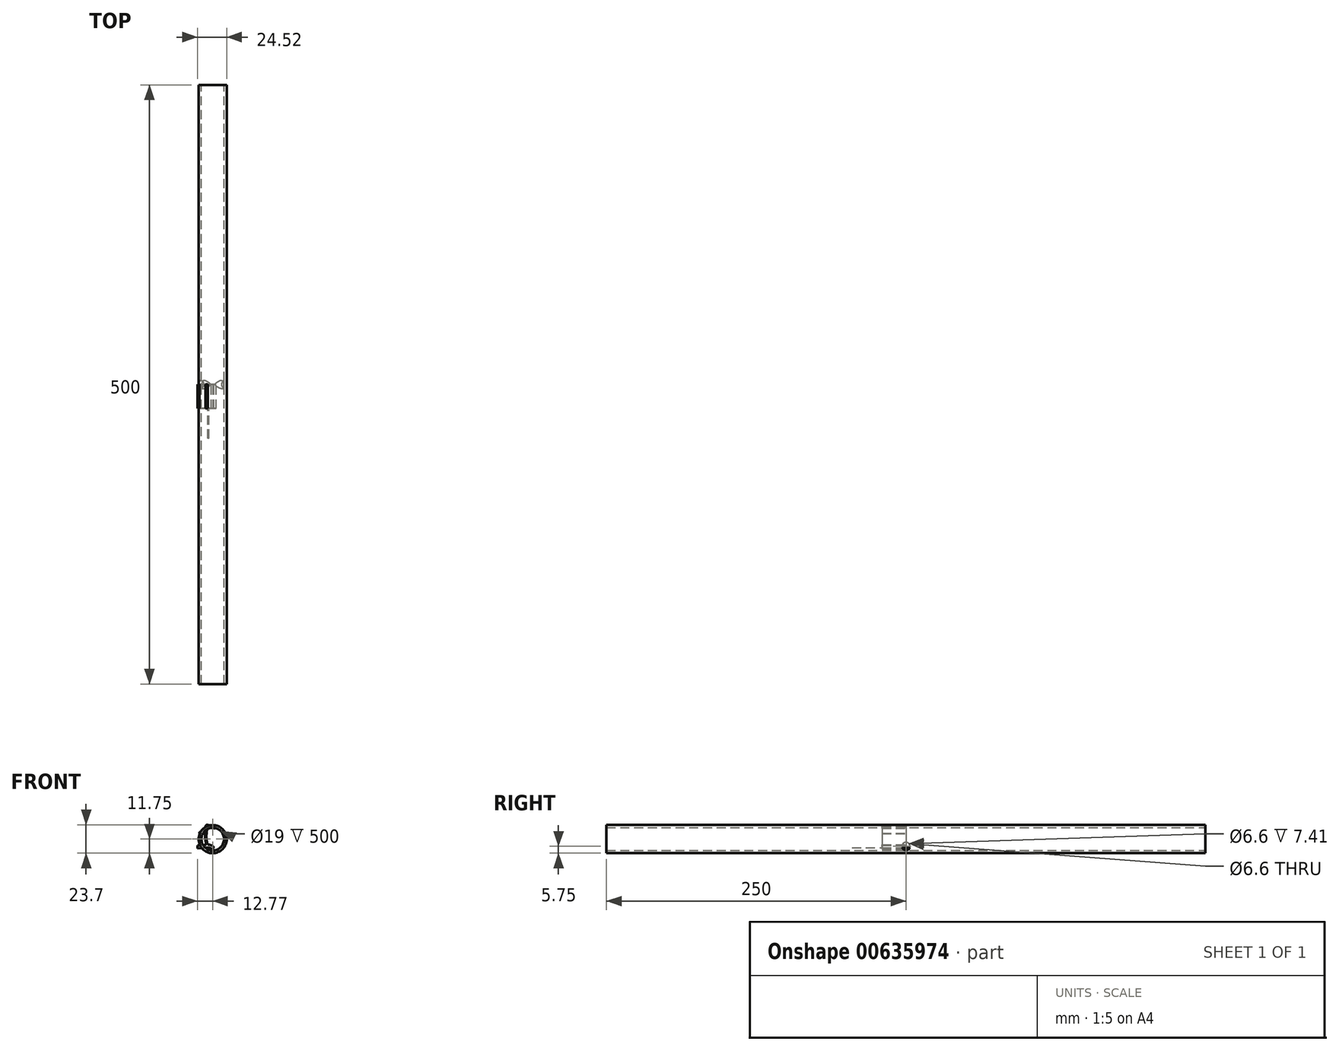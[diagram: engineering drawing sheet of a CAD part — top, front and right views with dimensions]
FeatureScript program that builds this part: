
annotation { "Feature Type Name" : "Feature", "Feature Type Description" : "" }
export const myFeature = defineFeature(function(context is Context, id is Id, definition is map)
    precondition{}
    {
        {
            var Q0;
            Q0=qCreatedBy(makeId("Front.planeOp"),FACE);
            var sketch = newSketch(context, id + "F0", { "sketchPlane" : qUnion([Q0])});
            skCircle(sketch, "E0", {"center": v(0, 0) * mm, "radius": 9.5 * mm});
            skCircle(sketch, "E1", {"center": v(0, 0) * mm, "radius": 11.75 * mm});
            skSolve(sketch);
        }
        {
            var Q0;
            Q0=makeQuery(id+"F0.imprint","IMPRINT",FACE,{"disambiguationData":[TD([[makeQuery(id+"F0.imprint","IMPRINT",EDGE,{"derivedFrom":sQuery(id+"F0.wireOp",EDGE,"E0")}),-1.0]])]});
            extrude(context, id + "F1", {"entities" : qUnion([Q0]), "depth" : 500 * mm, "offsetDistance" : 25 * mm, "symmetric" : true});
        }
        {
            var Q0;
            Q0=qCreatedBy(makeId("Front.planeOp"),FACE);
            var sketch = newSketch(context, id + "F2", { "sketchPlane" : qUnion([Q0])});
            skLineSegment(sketch, "E2.bottom", {"start": v(9.35, 12) * mm, "end": v(-9.35, 12) * mm});
            skLineSegment(sketch, "E2.top", {"start": v(9.35, -12) * mm, "end": v(-9.35, -12) * mm});
            skLineSegment(sketch, "E2.left", {"start": v(9.35, 12) * mm, "end": v(9.35, -12) * mm});
            skLineSegment(sketch, "E2.right", {"start": v(-9.35, 3.53) * mm, "end": v(-9.35, -12) * mm});
            skPoint(sketch, "E2.middle", {"position": v(0, 0) * mm});
            skLineSegment(sketch, "E3", {"start": v(-18.96, 6) * mm, "end": v(16.45, 6) * mm, "construction": true});
            skLineSegment(sketch, "E4", {"start": v(-9.35, 3.53) * mm, "end": v(-15.81, 7.76) * mm});
            skLineSegment(sketch, "E5", {"start": v(-15.81, 7.76) * mm, "end": v(-15.81, 12) * mm});
            skLineSegment(sketch, "E6", {"start": v(-15.81, 12) * mm, "end": v(-9.35, 12) * mm});
            skSolve(sketch);
        }
        {
            var Q0;
            Q0=makeQuery(id+"F2.imprint","IMPRINT",FACE,{"disambiguationData":[TD([[makeQuery(id+"F2.imprint","IMPRINT",EDGE,{"derivedFrom":sQuery(id+"F2.wireOp",EDGE,"E2.bottom")}),1.0]])]});
            extrude(context, id + "F3", {"entities" : qUnion([Q0]), "depth" : 12 * mm, "offsetDistance" : 25 * mm, "symmetric" : true});
        }
        {
            var Q0;
            Q0=makeQuery(id+"F3.opExtrude","SWEPT_FACE",FACE,{"disambiguationData":[OSD([sQuery(id+"F2.wireOp",EDGE,"E2.left")])]});
            var sketch = newSketch(context, id + "F4", { "sketchPlane" : qUnion([Q0])});
            skLineSegment(sketch, "E7", {"start": v(-13.9, -6) * mm, "end": v(15.88, -6) * mm, "construction": true});
            skLineSegment(sketch, "E8", {"start": v(0, -15.68) * mm, "end": v(0, 14.93) * mm, "construction": true});
            skCircle(sketch, "E9", {"center": v(0, -6) * mm, "radius": 3.3 * mm});
            skSolve(sketch);
        }
        {
            var Q0;
            Q0=makeQuery(id+"F4.imprint","IMPRINT",FACE,{"disambiguationData":[TD([[makeQuery(id+"F4.imprint","IMPRINT",EDGE,{"derivedFrom":sQuery(id+"F4.wireOp",EDGE,"E9")}),1.0]])]});
            extrude(context, id + "F5", {"entities" : qUnion([Q0]), "operationType" : NewBodyOperationType.REMOVE, "endBound" : BoundingType.THROUGH_ALL, "oppositeDirection" : true, "depth" : 25 * mm, "offsetDistance" : 25 * mm});
        }
        {
            var Q0;
            Q0=makeQuery(id+"F3.opExtrude","CAP_EDGE",EDGE,{"disambiguationData":[OSD([sQuery(id+"F2.wireOp",EDGE,"E4")])],"isStart":false});
            var Q1;
            Q1=makeQuery(id+"F3.opExtrude","CAP_EDGE",EDGE,{"disambiguationData":[OSD([sQuery(id+"F2.wireOp",EDGE,"E5")])],"isStart":false});
            var Q2;
            Q2=makeQuery(id+"F3.opExtrude","CAP_EDGE",EDGE,{"disambiguationData":[OSD([sQuery(id+"F2.wireOp",EDGE,"E2.bottom"),sQuery(id+"F2.wireOp",EDGE,"E6")])],"isStart":false});
            var Q3;
            Q3=makeQuery(id+"F3.opExtrude","CAP_EDGE",EDGE,{"disambiguationData":[OSD([sQuery(id+"F2.wireOp",EDGE,"E2.left")])],"isStart":false});
            var Q4;
            Q4=makeQuery(id+"F3.opExtrude","CAP_EDGE",EDGE,{"disambiguationData":[OSD([sQuery(id+"F2.wireOp",EDGE,"E2.top")])],"isStart":false});
            var Q5;
            Q5=makeQuery(id+"F3.opExtrude","CAP_EDGE",EDGE,{"disambiguationData":[OSD([sQuery(id+"F2.wireOp",EDGE,"E2.right")])],"isStart":false});
            var Q6;
            Q6=makeQuery(id+"F3.opExtrude","CAP_EDGE",EDGE,{"disambiguationData":[OSD([sQuery(id+"F2.wireOp",EDGE,"E4")])],"isStart":true});
            var Q7;
            Q7=makeQuery(id+"F3.opExtrude","CAP_EDGE",EDGE,{"disambiguationData":[OSD([sQuery(id+"F2.wireOp",EDGE,"E2.right")])],"isStart":true});
            var Q8;
            Q8=makeQuery(id+"F3.opExtrude","CAP_EDGE",EDGE,{"disambiguationData":[OSD([sQuery(id+"F2.wireOp",EDGE,"E2.top")])],"isStart":true});
            var Q9;
            Q9=makeQuery(id+"F3.opExtrude","CAP_EDGE",EDGE,{"disambiguationData":[OSD([sQuery(id+"F2.wireOp",EDGE,"E2.left")])],"isStart":true});
            var Q10;
            Q10=makeQuery(id+"F3.opExtrude","CAP_EDGE",EDGE,{"disambiguationData":[OSD([sQuery(id+"F2.wireOp",EDGE,"E2.bottom"),sQuery(id+"F2.wireOp",EDGE,"E6")])],"isStart":true});
            var Q11;
            Q11=makeQuery(id+"F3.opExtrude","CAP_EDGE",EDGE,{"disambiguationData":[OSD([sQuery(id+"F2.wireOp",EDGE,"E5")])],"isStart":true});
            var Q12;
            Q12=makeQuery(id+"F3.opExtrude","SWEPT_EDGE",EDGE,{"disambiguationData":[OSD([sQuery(id+"F2.wireOp",EDGE,"E2.bottom"),sQuery(id+"F2.wireOp",EDGE,"E2.left")])]});
            var Q13;
            Q13=makeQuery(id+"F3.opExtrude","SWEPT_EDGE",EDGE,{"disambiguationData":[OSD([sQuery(id+"F2.wireOp",EDGE,"E5"),sQuery(id+"F2.wireOp",EDGE,"E6")])]});
            var Q14;
            Q14=makeQuery(id+"F3.opExtrude","SWEPT_EDGE",EDGE,{"disambiguationData":[OSD([sQuery(id+"F2.wireOp",EDGE,"E2.top"),sQuery(id+"F2.wireOp",EDGE,"E2.right")])]});
            var Q15;
            Q15=makeQuery(id+"F3.opExtrude","SWEPT_EDGE",EDGE,{"disambiguationData":[OSD([sQuery(id+"F2.wireOp",EDGE,"E2.top"),sQuery(id+"F2.wireOp",EDGE,"E2.left")])]});
            var Q16;
            Q16=makeQuery(id+"F3.opExtrude","SWEPT_EDGE",EDGE,{"disambiguationData":[OSD([sQuery(id+"F2.wireOp",EDGE,"E4"),sQuery(id+"F2.wireOp",EDGE,"E5")])]});
            var Q17;
            Q17=makeQuery(id+"F3.opExtrude","SWEPT_EDGE",EDGE,{"disambiguationData":[OSD([sQuery(id+"F2.wireOp",EDGE,"E2.right"),sQuery(id+"F2.wireOp",EDGE,"E4")])]});
            fillet(context, id + "F6", {"entities" : qUnion([Q0, Q1, Q2, Q3, Q4, Q5, Q6, Q7, Q8, Q9, Q10, Q11, Q12, Q13, Q14, Q15, Q16, Q17]), "radius" : 1 * mm, "tangentPropagation" : true, "allowEdgeOverflow" : false});
        }
        {
            var Q0;
            Q0=qCreatedBy(makeId("Front.planeOp"),FACE);
            var sketch = newSketch(context, id + "F7", { "sketchPlane" : qUnion([Q0])});
            skLineSegment(sketch, "E10.bottom", {"start": v(4.25, 9.5) * mm, "end": v(-4.25, 9.5) * mm, "construction": true});
            skLineSegment(sketch, "E10.top", {"start": v(4.25, -9.5) * mm, "end": v(-4.25, -9.5) * mm, "construction": true});
            skLineSegment(sketch, "E10.left", {"start": v(4.25, 9.5) * mm, "end": v(4.25, -9.5) * mm, "construction": true});
            skLineSegment(sketch, "E10.right", {"start": v(-4.25, 9.5) * mm, "end": v(-4.25, -4.65) * mm, "construction": true});
            skPoint(sketch, "E10.middle", {"position": v(0, 0) * mm});
            skLineSegment(sketch, "E11.0", {"start": v(3.75, 9) * mm, "end": v(-3.75, 9) * mm, "construction": true});
            skLineSegment(sketch, "E11.1", {"start": v(3.75, 9) * mm, "end": v(3.75, -9) * mm, "construction": true});
            skLineSegment(sketch, "E11.2", {"start": v(3.75, -9) * mm, "end": v(-3.73, -9) * mm, "construction": true});
            skLineSegment(sketch, "E11.3", {"start": v(-3.75, 9) * mm, "end": v(-3.75, -4) * mm, "construction": true});
            skLineSegment(sketch, "E12", {"start": v(-3.75, -4.65) * mm, "end": v(0.77, -4.65) * mm, "construction": true});
            skLineSegment(sketch, "E13", {"start": v(0.77, -4.65) * mm, "end": v(0.77, -8.36) * mm, "construction": true});
            skLineSegment(sketch, "E14", {"start": v(0.77, -8.36) * mm, "end": v(-4.25, -7.75) * mm, "construction": true});
            skLineSegment(sketch, "E15.trimOffspring", {"start": v(-4.25, -7.75) * mm, "end": v(-4.25, -9.5) * mm, "construction": true});
            skLineSegment(sketch, "E16.0", {"start": v(-8.27, -9.5) * mm, "end": v(9.76, -9.5) * mm});
            skLineSegment(sketch, "E17.0", {"start": v(-3.75, -4) * mm, "end": v(1.28, -4) * mm, "construction": true});
            skArc(sketch, "E18", {"start": v(-0.65, -8.19) * mm, "mid": v(0.66, -7.4) * mm, "end": v(0.23, -5.93) * mm});
            skLineSegment(sketch, "E19.0", {"start": v(0.7, -8.85) * mm, "end": v(-3.73, -8.32) * mm, "construction": true});
            skLineSegment(sketch, "E20", {"start": v(-4.25, -4.65) * mm, "end": v(-3.75, -4.65) * mm, "construction": true});
            skLineSegment(sketch, "E21.trimOffspring", {"start": v(-3.73, -8.32) * mm, "end": v(-3.73, -9) * mm, "construction": true});
            skLineSegment(sketch, "E22", {"start": v(0.7, -8.85) * mm, "end": v(1.28, -8.85) * mm, "construction": true});
            skLineSegment(sketch, "E23.trimOffspring", {"start": v(1.28, -4) * mm, "end": v(1.28, -8.85) * mm, "construction": true});
            skLineSegment(sketch, "E24", {"start": v(-5.25, -10.27) * mm, "end": v(-5.25, 10.17) * mm, "construction": true});
            skArc(sketch, "E25", {"start": v(0.23, -5.93) * mm, "mid": v(-1.66, -4.98) * mm, "end": v(-3.75, -4.65) * mm});
            skPoint(sketch, "E26", {"position": v(-5.25, 2.43) * mm});
            skPoint(sketch, "E26.positionSnap0", {"position": v(-4.25, 2.43) * mm});
            skArc(sketch, "E27", {"start": v(-4.25, 9.5) * mm, "mid": v(-5.25, 2.43) * mm, "end": v(-4.25, -4.65) * mm});
            skArc(sketch, "E28.0", {"start": v(-6.17, 4.53) * mm, "mid": v(-6.12, -0.17) * mm, "end": v(-5.25, -4.79) * mm});
            skArc(sketch, "E29", {"start": v(-1.38, -7.83) * mm, "mid": v(0.45, -7.75) * mm, "end": v(0.23, -5.93) * mm});
            skArc(sketch, "E30.0", {"start": v(-1.22, -7.94) * mm, "mid": v(-2.57, -7.29) * mm, "end": v(-4.07, -7.14) * mm});
            skLineSegment(sketch, "E31", {"start": v(-4.07, -7.14) * mm, "end": v(-4.25, -4.65) * mm, "construction": true});
            skLineSegment(sketch, "E32", {"start": v(-4.07, -7.14) * mm, "end": v(-11.18, -7.66) * mm});
            skLineSegment(sketch, "E33", {"start": v(-5.25, -4.79) * mm, "end": v(-12.77, -5.34) * mm});
            skArc(sketch, "E34", {"start": v(-4.25, 9.5) * mm, "mid": v(-3.69, 9.84) * mm, "end": v(-3.38, 10.41) * mm});
            skLineSegment(sketch, "E35", {"start": v(-4.25, -4.65) * mm, "end": v(-3.75, -4.65) * mm});
            skLineSegment(sketch, "E36", {"start": v(-12.77, -5.34) * mm, "end": v(-12.6, -7.76) * mm});
            skLineSegment(sketch, "E37", {"start": v(-11.18, -7.66) * mm, "end": v(-12.6, -7.76) * mm});
            skArc(sketch, "E38.trimOffspring", {"start": v(-3.98, 11.8) * mm, "mid": v(-5.67, 11.34) * mm, "end": v(-5.25, 9.64) * mm});
            skArc(sketch, "E39", {"start": v(0.3, 9.87) * mm, "mid": v(2.63, 9.72) * mm, "end": v(1.03, 11.4) * mm});
            skArc(sketch, "E40.0", {"start": v(-3.38, 10.41) * mm, "mid": v(-1.56, 9.94) * mm, "end": v(0.3, 9.87) * mm});
            skLineSegment(sketch, "E41", {"start": v(-5.25, 9.64) * mm, "end": v(-10.87, 5.78) * mm});
            skArc(sketch, "E42.filletArc", {"start": v(-10.87, 5.78) * mm, "mid": v(-11.06, 5.2) * mm, "end": v(-10.55, 4.87) * mm});
            skLineSegment(sketch, "E43", {"start": v(-10.55, 4.87) * mm, "end": v(-6.17, 4.53) * mm});
            skArc(sketch, "E44", {"start": v(-3.98, 11.8) * mm, "mid": v(-1.53, 10.97) * mm, "end": v(1.03, 11.4) * mm});
            skSolve(sketch);
        }
        {
            var Q0;
            {var subQ4=sQuery(id+"F7.wireOp",EDGE,"E25");Q0=makeQuery(id+"F7.imprint","IMPRINT",FACE,{"disambiguationData":[TD([[makeQuery(id+"F7.imprint","IMPRINT",EDGE,{"derivedFrom":subQ4}),1.0]])]});}
            extrude(context, id + "F8", {"entities" : qUnion([Q0]), "depth" : 20 * mm, "offsetDistance" : 25 * mm});
        }
        {
            var Q0;
            Q0=makeQuery(id+"F8.opExtrude","SWEPT_BODY",BODY,{"disambiguationData":[OSD([sQuery(id+"F7.wireOp",EDGE,"E25"),sQuery(id+"F7.wireOp",EDGE,"E27"),sQuery(id+"F7.wireOp",EDGE,"E28.0"),sQuery(id+"F7.wireOp",EDGE,"E29"),sQuery(id+"F7.wireOp",EDGE,"E30.0"),sQuery(id+"F7.wireOp",EDGE,"E32"),sQuery(id+"F7.wireOp",EDGE,"E33"),sQuery(id+"F7.wireOp",EDGE,"E34"),sQuery(id+"F7.wireOp",EDGE,"E35"),sQuery(id+"F7.wireOp",EDGE,"E36"),sQuery(id+"F7.wireOp",EDGE,"E37"),sQuery(id+"F7.wireOp",EDGE,"E38.trimOffspring"),sQuery(id+"F7.wireOp",EDGE,"E39"),sQuery(id+"F7.wireOp",EDGE,"E40.0"),sQuery(id+"F7.wireOp",EDGE,"E41"),sQuery(id+"F7.wireOp",EDGE,"E42.filletArc"),sQuery(id+"F7.wireOp",EDGE,"E43"),sQuery(id+"F7.wireOp",EDGE,"E44")])]});
            transform(context, id + "F9", {"entities" : qUnion([Q0]), "transformType" : TransformType.TRANSLATION_3D, "dx" : 0 * mm, "dy" : 0 * mm, "dz" : 0 * mm, "makeCopy" : true});
        }
        {
            var Q0;
            Q0=makeQuery(id+"F9.opPattern","COPY",FACE,{"derivedFrom":makeQuery(id+"F8.opExtrude","CAP_FACE",FACE,{"disambiguationData":[OSD([sQuery(id+"F7.wireOp",EDGE,"E25"),sQuery(id+"F7.wireOp",EDGE,"E27"),sQuery(id+"F7.wireOp",EDGE,"E28.0"),sQuery(id+"F7.wireOp",EDGE,"E29"),sQuery(id+"F7.wireOp",EDGE,"E30.0"),sQuery(id+"F7.wireOp",EDGE,"E32"),sQuery(id+"F7.wireOp",EDGE,"E33"),sQuery(id+"F7.wireOp",EDGE,"E34"),sQuery(id+"F7.wireOp",EDGE,"E35"),sQuery(id+"F7.wireOp",EDGE,"E36"),sQuery(id+"F7.wireOp",EDGE,"E37"),sQuery(id+"F7.wireOp",EDGE,"E38.trimOffspring"),sQuery(id+"F7.wireOp",EDGE,"E39"),sQuery(id+"F7.wireOp",EDGE,"E40.0"),sQuery(id+"F7.wireOp",EDGE,"E41"),sQuery(id+"F7.wireOp",EDGE,"E42.filletArc"),sQuery(id+"F7.wireOp",EDGE,"E43"),sQuery(id+"F7.wireOp",EDGE,"E44")])],"isStart":false}),"instanceName":"1"});
            var sketch = newSketch(context, id + "F10", { "sketchPlane" : qUnion([Q0])});
            skPoint(sketch, "E45.0", {"position": v(-4.25, -7.75) * mm});
            skPoint(sketch, "E46.0", {"position": v(-6.17, 4.53) * mm});
            skArc(sketch, "E47", {"start": v(-4.83, -6.3) * mm, "mid": v(-2.37, -6.4) * mm, "end": v(-4.25, -4.82) * mm});
            skPoint(sketch, "E47.second.point", {"position": v(-3.75, -4.65) * mm});
            skPoint(sketch, "E47.third.point", {"position": v(-2.32, -6.26) * mm});
            skArc(sketch, "E48", {"start": v(-6.17, 4.53) * mm, "mid": v(-5.98, -0.94) * mm, "end": v(-4.83, -6.3) * mm});
            skArc(sketch, "E49", {"start": v(-4.25, 9.5) * mm, "mid": v(-5.27, 2.34) * mm, "end": v(-4.25, -4.82) * mm});
            skLineSegment(sketch, "E50", {"start": v(-5.25, 9.64) * mm, "end": v(-10.87, 5.78) * mm});
            skLineSegment(sketch, "E51", {"start": v(-10.55, 4.87) * mm, "end": v(-6.17, 4.53) * mm});
            skArc(sketch, "E52", {"start": v(-3.84, 11.7) * mm, "mid": v(-5.62, 11.4) * mm, "end": v(-5.25, 9.64) * mm});
            skArc(sketch, "E53", {"start": v(0.3, 9.87) * mm, "mid": v(2.65, 9.76) * mm, "end": v(0.94, 11.37) * mm});
            skArc(sketch, "E54", {"start": v(-3.98, 11.8) * mm, "mid": v(-1.53, 10.94) * mm, "end": v(1.03, 11.4) * mm});
            skArc(sketch, "E55", {"start": v(-3.38, 10.41) * mm, "mid": v(-1.57, 9.92) * mm, "end": v(0.3, 9.87) * mm});
            skArc(sketch, "E56", {"start": v(-10.87, 5.78) * mm, "mid": v(-11, 5.22) * mm, "end": v(-10.55, 4.87) * mm});
            skArc(sketch, "E57.trimOffspring", {"start": v(-4.25, 9.5) * mm, "mid": v(-3.69, 9.84) * mm, "end": v(-3.38, 10.41) * mm});
            skSolve(sketch);
        }
        {
            var Q0;
            {var subQ19=sQuery(id+"F10.wireOp",EDGE,"E49");Q0=makeQuery(id+"F10.imprint","IMPRINT",FACE,{"disambiguationData":[TD([[makeQuery(id+"F10.imprint","IMPRINT",EDGE,{"derivedFrom":subQ19}),-1.0]])]});}
            var Q1;
            {var subQ0=sQuery(id+"F10.wireOp",EDGE,"E47");var subQ1=makeQuery(id+"F9.opPattern","COPY",EDGE,{"derivedFrom":makeQuery(id+"F8.opExtrude","CAP_EDGE",EDGE,{"disambiguationData":[OSD([sQuery(id+"F7.wireOp",EDGE,"E30.0")])],"isStart":false}),"instanceName":"1"});var subQ3=makeQuery(id+"F10.imprint","INTERSECT",VERTEX,{"derivedFrom":[subQ1,subQ0]});Q1=makeQuery(id+"F10.imprint","IMPRINT",FACE,{"disambiguationData":[TD([[makeQuery(id+"F10.imprint","IMPRINT",EDGE,{"disambiguationData":[TD([[subQ3,1.0]])],"derivedFrom":subQ0}),1.0]])]});}
            extrude(context, id + "F11", {"entities" : qUnion([Q0, Q1]), "depth" : 25 * mm, "offsetDistance" : 25 * mm});
        }
        {
            var Q0;
            Q0=makeQuery(id+"F3.opExtrude","SWEPT_BODY",BODY,{"disambiguationData":[OSD([sQuery(id+"F2.wireOp",EDGE,"E2.bottom"),sQuery(id+"F2.wireOp",EDGE,"E2.top"),sQuery(id+"F2.wireOp",EDGE,"E2.left"),sQuery(id+"F2.wireOp",EDGE,"E2.right"),sQuery(id+"F2.wireOp",EDGE,"E4"),sQuery(id+"F2.wireOp",EDGE,"E5"),sQuery(id+"F2.wireOp",EDGE,"E6")])]});
            deleteBodies(context, id + "F12", {"entities" : qUnion([Q0])});
        }
    });
